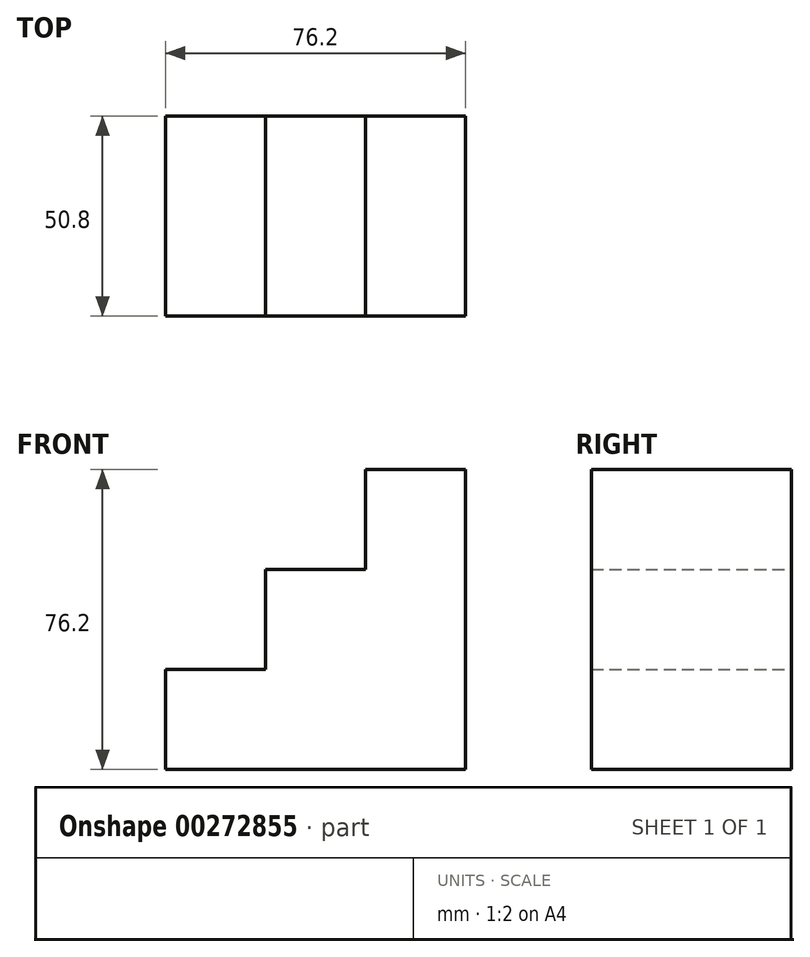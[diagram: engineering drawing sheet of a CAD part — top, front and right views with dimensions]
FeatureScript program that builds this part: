
annotation { "Feature Type Name" : "Feature", "Feature Type Description" : "" }
export const myFeature = defineFeature(function(context is Context, id is Id, definition is map)
    precondition{}
    {
        {
            var Q0;
            Q0=qCreatedBy(makeId("Front.planeOp"),FACE);
            var sketch = newSketch(context, id + "F0", { "sketchPlane" : qUnion([Q0])});
            skLineSegment(sketch, "E0", {"start": v(0, 0) * mm, "end": v(0, 76.2) * mm});
            skLineSegment(sketch, "E1", {"start": v(0, 0) * mm, "end": v(-76.2, 0) * mm});
            skLineSegment(sketch, "E2", {"start": v(0, 76.2) * mm, "end": v(-25.4, 76.2) * mm});
            skLineSegment(sketch, "E3", {"start": v(-25.4, 76.2) * mm, "end": v(-25.4, 50.8) * mm});
            skLineSegment(sketch, "E4", {"start": v(-25.4, 50.8) * mm, "end": v(-50.8, 50.8) * mm});
            skLineSegment(sketch, "E5", {"start": v(-50.8, 50.8) * mm, "end": v(-50.8, 25.4) * mm});
            skLineSegment(sketch, "E6", {"start": v(-50.8, 25.4) * mm, "end": v(-76.2, 25.4) * mm});
            skLineSegment(sketch, "E7", {"start": v(-76.2, 25.4) * mm, "end": v(-76.2, 0) * mm});
            skSolve(sketch);
        }
        {
            var Q0;
            Q0 = qSketchRegion(id + "F0", true);
            extrude(context, id + "F1", {"entities" : qUnion([Q0]), "depth" : 50.8 * mm});
        }
    });
